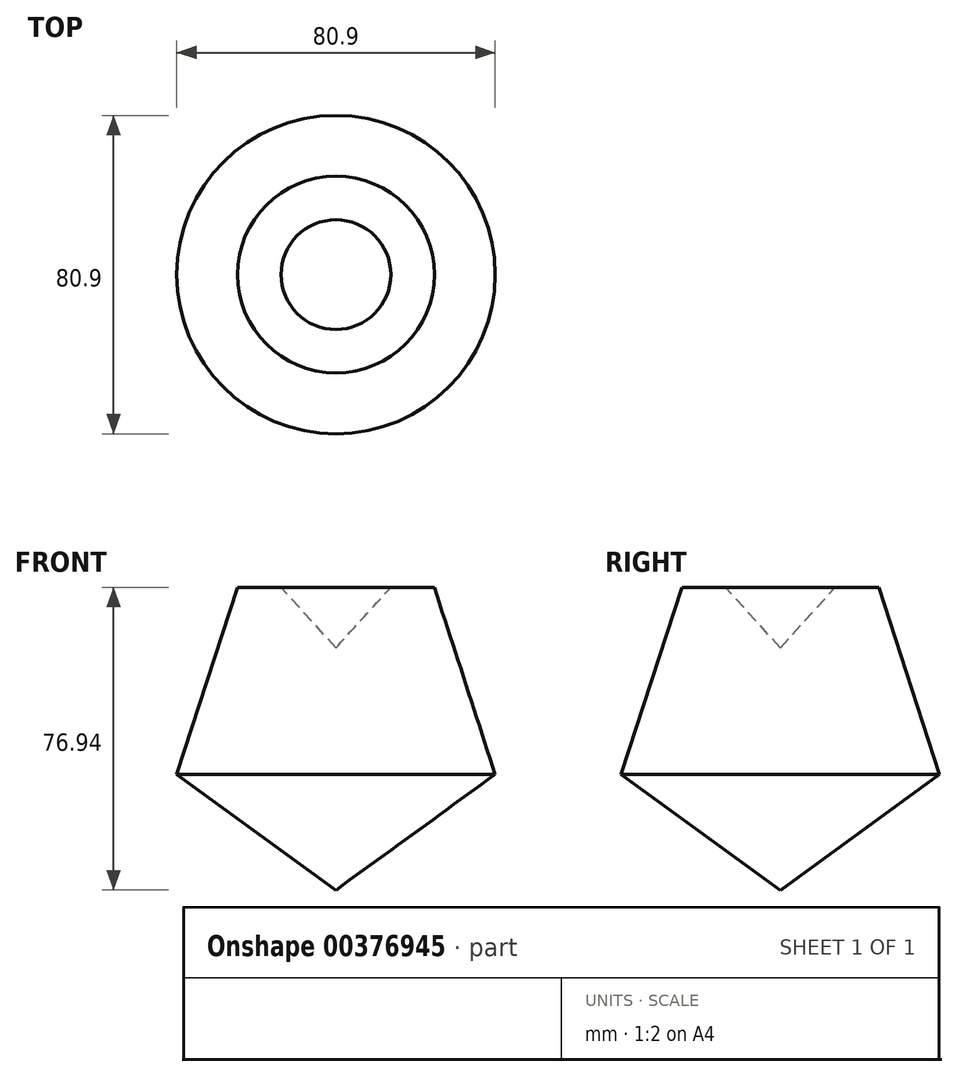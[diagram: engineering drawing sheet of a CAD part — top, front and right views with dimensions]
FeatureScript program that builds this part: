
annotation { "Feature Type Name" : "Feature", "Feature Type Description" : "" }
export const myFeature = defineFeature(function(context is Context, id is Id, definition is map)
    precondition{}
    {
        {
            var Q0;
            Q0=qCreatedBy(makeId("Front.planeOp"),FACE);
            var sketch = newSketch(context, id + "F0", { "sketchPlane" : qUnion([Q0])});
            skCircle(sketch, "E0.cCircle", {"center": v(0, 0) * mm, "radius": 34.4 * mm, "construction": true});
            skLineSegment(sketch, "E0.0", {"start": v(-25, 34.4) * mm, "end": v(-13.94, 34.4) * mm});
            skLineSegment(sketch, "E0.1", {"start": v(25, 34.4) * mm, "end": v(40.45, -13.14) * mm});
            skLineSegment(sketch, "E0.2", {"start": v(40.45, -13.14) * mm, "end": v(0, -42.53) * mm});
            skLineSegment(sketch, "E0.3", {"start": v(0, -42.53) * mm, "end": v(-40.45, -13.14) * mm});
            skLineSegment(sketch, "E0.4", {"start": v(-40.45, -13.14) * mm, "end": v(-25, 34.4) * mm});
            skPoint(sketch, "E0.0.midPoint", {"position": v(0, 34.4) * mm});
            skLineSegment(sketch, "E1", {"start": v(-13.94, 34.4) * mm, "end": v(0, 19.02) * mm});
            skLineSegment(sketch, "E2", {"start": v(0, 19.02) * mm, "end": v(17, 34.4) * mm});
            skLineSegment(sketch, "E3.trimOffspring", {"start": v(17, 34.4) * mm, "end": v(25, 34.4) * mm});
            skLineSegment(sketch, "E4", {"start": v(0, 19.02) * mm, "end": v(0, -42.53) * mm});
            skSolve(sketch);
        }
        {
            var Q0;
            Q0=makeQuery(id+"F0.imprint","IMPRINT",FACE,{"disambiguationData":[TD([[makeQuery(id+"F0.imprint","IMPRINT",EDGE,{"derivedFrom":sQuery(id+"F0.wireOp",EDGE,"E0.0")}),-1.0]])]});
            var Q1;
            Q1=sQuery(id+"F0.wireOp",EDGE,"E4");
            revolve(context, id + "F1", {"entities" : qUnion([Q0]), "axis" : qUnion([Q1]), "revolveType" : RevolveType.FULL});
        }
    });
